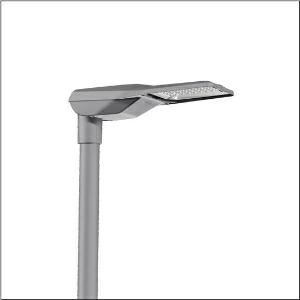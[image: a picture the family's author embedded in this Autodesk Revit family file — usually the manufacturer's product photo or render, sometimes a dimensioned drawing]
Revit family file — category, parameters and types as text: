
# Revit family: streetlight_sl_21_iq_mini___st0_8a_5xe2c21d08hb_7297
name_source: partatom
category: Lighting Fixtures
units: mm (PartAtom-declared; Revit-internal decimal feet)

## family parameters
Cut with Voids When Loaded = No
Host = Face
Light Source = No
Part Type = Normal
Room Calculation Point = No
Round Connector Dimension = Use Diameter
Shared = No

## types (1)
- --- (1 x LED, 7830 lm, 70.9 W, 2200K)
    Apparent Load = 71 VA
    CIE Flux Codes = 38 75 97 100 100
    Color Rendering = 70
    Color Temperature = 2200K
    Default Elevation = 1800 mm
    Description = Streetlight SL 21 iQ mini, mast luminaire, primary light control with lens, of PMMA, primary optical cover: cover, of toughened safety glass, transparent, light distribution: ST0.8a, light emission: direct distribution, primary light characteristic: asymmetric, installation type: post-top, side-entry, LED, High Power LED, rated luminous flux: 7.830lm, luminous efficacy: 110lm/W, light colour: 722, colour temperature: 2200K, control: Auto-Match, Temp-Guard, Lumen-Switch, Night-Set, Smart-Wire, Light-Fading, Desk-Remote (wireless, voltage-free reading and setting of iQ features in the workshop via application-optimized NFC function/RFID function), optimised constant luminous flux control (CLO 2.0), pre-setting: linear dimming characteristic, mains connection: 220..240V, AC, 50/60Hz, start of lifetime: 71W, end of service life: 75W, reduction: 31W, luminaire housing, of diecast aluminium, powder-coated, Siteco® metallic grey (DB 702S), corrosivity category C5 mid according to DIN EN ISO 12944, please order mast flange separately, inclination adjustable: 0°, 5°, 10°, 15°, sealing non-destructively replaceable, multi-level sealing system, length: 628mm, width: 235mm, height: 110mm, mast flange for spigot size: 42mm (side-entry): 5XC10008XM4, 60/48mm (side-entry/post-top): 5XC10108XM2, 76/60mm (side-entry/post-top): 5XC10108XM1, protection rating (complete): IP66, insulation class (complete): insulation class II (safety insulation), certification: CE, ENEC, ENEC+, VDE, impact resistance: IK09, permissible operating ambient temperature for outdoor applications: -40..+50°C, standard-compliant lighting for roads and squares, packaging unit: 1 piece

Light Distribution: ST0.8a
    Height = 110 mm
    Lamp = 1 x LED
    Lamp Light Flux = 7830 lm
    Lamp Power = 70.9 W
    Lamp count = 1
    Length = 625 mm
    Luminous efficacy = 110 lm/W
    Manufacturer = Siteco
    ModVariant = No
    Model = 5XE2C21D08HB
    Number of Poles = 1
    OnlyDefault = Yes
    Power Factor = 1
    Product Name = Streetlight SL 21 iQ mini | ST0.8a
    Product group = mast luminaire | pylon top
    ProductGroupID = 6100
    Protection Class = Protection class II
    Protection Degree = IP 66
    RLX_Detail_Level = 1
    RLX_Emergency_Light_Flux = 0 lm
    RLX_Emergency_Type = 0
    RLX_Emergency_Type_DB = No
    RlxData = <blob elided: 93761 chars, md5=f528737f>
    Socket = socket
    Standby Power = 0 W
    System Light Flux = 7830 lm
    System Power = 71 W
    Type Comments = factory setting: luminous flux: 100 % | dim-lin: 254 | 711 mA
    Type Image = l_1003519.jpg
    URL = http://relux.com
    VarID = @adj_127913
    Voltage = 0 V
    Weight = 0.00 kg
    Width = 234 mm

## geometry (parser evidence)
native form markers: Blend x4, Sweep x10
no freeform markers — native parametric forms only
